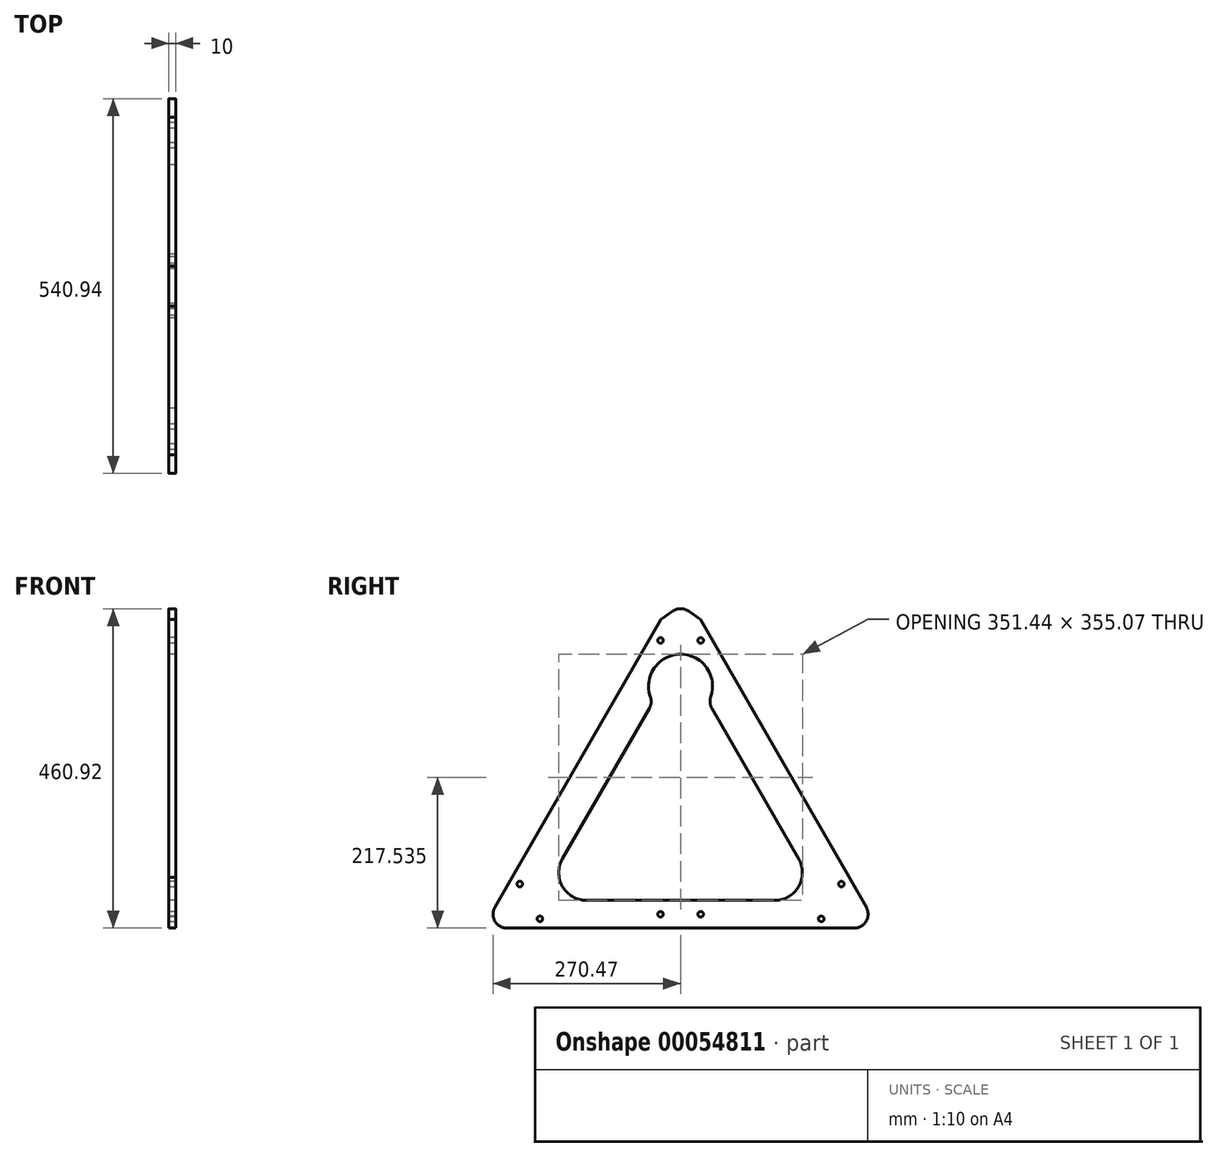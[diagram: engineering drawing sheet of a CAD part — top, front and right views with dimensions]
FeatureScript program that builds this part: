
annotation { "Feature Type Name" : "Feature", "Feature Type Description" : "" }
export const myFeature = defineFeature(function(context is Context, id is Id, definition is map)
    precondition{}
    {
        {
            var Q0;
            Q0=qCreatedBy(makeId("Right.planeOp"),FACE);
            var sketch = newSketch(context, id + "F0", { "sketchPlane" : qUnion([Q0])});
            skLineSegment(sketch, "E0", {"start": v(-103.88, 0) * mm, "end": v(158.82, 0) * mm, "construction": true});
            skLineSegment(sketch, "E1", {"start": v(0, 81.5) * mm, "end": v(0, -83.4) * mm, "construction": true});
            skLineSegment(sketch, "E2.0", {"start": v(-145, 81.5) * mm, "end": v(-145, -83.4) * mm, "construction": true});
            skLineSegment(sketch, "E3.0", {"start": v(-205, 81.5) * mm, "end": v(-205, -83.4) * mm, "construction": true});
            skLineSegment(sketch, "E4.0", {"start": v(-145, -40) * mm, "end": v(145, -40) * mm, "construction": true});
            skLineSegment(sketch, "E5", {"start": v(0, 0) * mm, "end": v(-205, 0) * mm, "construction": true});
            skLineSegment(sketch, "E6", {"start": v(-205, 0) * mm, "end": v(-195.15, 17.07) * mm, "construction": true});
            skLineSegment(sketch, "E7", {"start": v(-205, 0) * mm, "end": v(-200.07, 8.53) * mm, "construction": true});
            skLineSegment(sketch, "E8", {"start": v(-200.07, 8.53) * mm, "end": v(14.56, 380.29) * mm, "construction": true});
            skLineSegment(sketch, "E9", {"start": v(0, 0) * mm, "end": v(0, 452.2) * mm, "construction": true});
            skSolve(sketch);
        }
        {
            var Q0;
            Q0=qCreatedBy(makeId("Right.planeOp"),FACE);
            var sketch = newSketch(context, id + "F1", { "sketchPlane" : qUnion([Q0])});
            skLineSegment(sketch, "E10.0", {"start": v(0, 0) * mm, "end": v(-205, 0) * mm});
            skLineSegment(sketch, "E11.0", {"start": v(-200.07, 8.53) * mm, "end": v(0, 355.07) * mm});
            skLineSegment(sketch, "E12.0", {"start": v(-145, -40) * mm, "end": v(145, -40) * mm});
            skLineSegment(sketch, "E13.0", {"start": v(0, 81.5) * mm, "end": v(0, 0) * mm});
            skLineSegment(sketch, "E14", {"start": v(0, -83.4) * mm, "end": v(0, 81.5) * mm, "construction": true});
            skLineSegment(sketch, "E15", {"start": v(0, -40) * mm, "end": v(-384.65, -40) * mm, "construction": true});
            skLineSegment(sketch, "E16.0", {"start": v(-243.37, 33.53) * mm, "end": v(-28.74, 405.29) * mm, "construction": true});
            skLineSegment(sketch, "E17", {"start": v(-145, -40) * mm, "end": v(-284.62, -40) * mm, "construction": true});
            skLineSegment(sketch, "E18", {"start": v(-284.62, -40) * mm, "end": v(-243.37, 33.53) * mm});
            skLineSegment(sketch, "E19", {"start": v(-243.37, 33.53) * mm, "end": v(-28.74, 405.29) * mm});
            skLineSegment(sketch, "E20", {"start": v(-28.74, 405.29) * mm, "end": v(0, 425.28) * mm});
            skLineSegment(sketch, "E21", {"start": v(-200.07, 8.53) * mm, "end": v(-205, 0) * mm});
            skLineSegment(sketch, "E22", {"start": v(-44.8, 433.21) * mm, "end": v(-37.84, 423.2) * mm});
            skLineSegment(sketch, "E23", {"start": v(-284.62, -40) * mm, "end": v(0, -40) * mm});
            skLineSegment(sketch, "E24.MirrorCS", {"start": v(243.37, 33.53) * mm, "end": v(28.74, 405.29) * mm});
            skLineSegment(sketch, "E25.MirrorCS", {"start": v(28.74, 405.29) * mm, "end": v(0, 425.28) * mm});
            skLineSegment(sketch, "E26.MirrorCS", {"start": v(200.07, 8.53) * mm, "end": v(0, 355.07) * mm});
            skLineSegment(sketch, "E27.MirrorCS", {"start": v(284.62, -40) * mm, "end": v(243.37, 33.53) * mm});
            skLineSegment(sketch, "E28.MirrorCS", {"start": v(284.62, -40) * mm, "end": v(0, -40) * mm});
            skLineSegment(sketch, "E29.MirrorCS", {"start": v(0, 0) * mm, "end": v(205, 0) * mm});
            skLineSegment(sketch, "E30.MirrorCS", {"start": v(200.07, 8.53) * mm, "end": v(205, 0) * mm});
            skLineSegment(sketch, "E31.trimOffspring", {"start": v(0, -40) * mm, "end": v(0, -83.4) * mm});
            skPoint(sketch, "E32.orphan", {"position": v(-14.56, 380.29) * mm});
            skPoint(sketch, "E33.orphan", {"position": v(14.56, 380.29) * mm});
            skLineSegment(sketch, "E34", {"start": v(0, 355.07) * mm, "end": v(-80.62, 355.07) * mm, "construction": true});
            skLineSegment(sketch, "E35", {"start": v(0, 355.07) * mm, "end": v(0, 406.28) * mm, "construction": true});
            skLineSegment(sketch, "E36.0", {"start": v(-29, 355.07) * mm, "end": v(-29, 406.28) * mm, "construction": true});
            skLineSegment(sketch, "E37", {"start": v(0, 355.07) * mm, "end": v(0, 0) * mm, "construction": true});
            skLineSegment(sketch, "E38", {"start": v(0, 177.54) * mm, "end": v(340.97, 177.54) * mm, "construction": true});
            skLineSegment(sketch, "E39.0", {"start": v(-40, 355.07) * mm, "end": v(-40, 0) * mm, "construction": true});
            skLineSegment(sketch, "E40", {"start": v(-40, 285.79) * mm, "end": v(0, 285.79) * mm, "construction": true});
            skLineSegment(sketch, "E41.0", {"start": v(-40, 335.79) * mm, "end": v(0, 335.79) * mm, "construction": true});
            skArc(sketch, "E42", {"start": v(0, 355.07) * mm, "mid": v(-40, 331.98) * mm, "end": v(-40, 285.79) * mm});
            skArc(sketch, "E43.MirrorCS", {"start": v(0, 355.07) * mm, "mid": v(40, 331.98) * mm, "end": v(40, 285.79) * mm});
            skLineSegment(sketch, "E44.0", {"start": v(0, 375.07) * mm, "end": v(-80.62, 375.07) * mm, "construction": true});
            skCircle(sketch, "E45", {"center": v(-29, 375.07) * mm, "radius": 4 * mm});
            skCircle(sketch, "E46.MirrorC", {"center": v(29, 375.07) * mm, "radius": 4 * mm});
            skCircle(sketch, "E47.1.0", {"center": v(-231.93, 23.58) * mm, "radius": 4 * mm});
            skCircle(sketch, "E47.1.1", {"center": v(-202.93, -26.65) * mm, "radius": 4 * mm});
            skCircle(sketch, "E47.2.0", {"center": v(202.93, -26.65) * mm, "radius": 4 * mm});
            skCircle(sketch, "E47.2.1", {"center": v(231.93, 23.58) * mm, "radius": 4 * mm});
            skPoint(sketch, "E47.center", {"position": v(0, 124) * mm});
            skPoint(sketch, "E48.MirrorP", {"position": v(14.56, -25.22) * mm});
            skPoint(sketch, "E49.MirrorP", {"position": v(-14.56, -25.22) * mm});
            skCircle(sketch, "E50.MirrorC", {"center": v(29, -20) * mm, "radius": 4 * mm});
            skCircle(sketch, "E51.MirrorC", {"center": v(-29, -20) * mm, "radius": 4 * mm});
            skSolve(sketch);
        }
        {
            var Q0;
            Q0=makeQuery(id+"F1.imprint","IMPRINT",FACE,{"disambiguationData":[TD([[makeQuery(id+"F1.imprint","IMPRINT",EDGE,{"derivedFrom":sQuery(id+"F1.wireOp",EDGE,"E10.0")}),1.0]])]});
            extrude(context, id + "F2", {"entities" : qUnion([Q0]), "depth" : 10 * mm, "offsetDistance" : 25 * mm});
        }
        {
            var Q0;
            Q0=makeQuery(id+"F2.opExtrude","SWEPT_EDGE",EDGE,{"disambiguationData":[OSD([sQuery(id+"F1.wireOp",EDGE,"E18"),sQuery(id+"F1.wireOp",EDGE,"E23")])]});
            var Q1;
            Q1=makeQuery(id+"F2.opExtrude","SWEPT_EDGE",EDGE,{"disambiguationData":[OSD([sQuery(id+"F1.wireOp",EDGE,"E27.MirrorCS"),sQuery(id+"F1.wireOp",EDGE,"E28.MirrorCS")])]});
            var Q2;
            Q2=makeQuery(id+"F2.opExtrude","SWEPT_EDGE",EDGE,{"disambiguationData":[OSD([sQuery(id+"F1.wireOp",EDGE,"E20"),sQuery(id+"F1.wireOp",EDGE,"E25.MirrorCS")])]});
            var Q3;
            Q3=makeQuery(id+"F2.opExtrude","SWEPT_EDGE",EDGE,{"disambiguationData":[OSD([sQuery(id+"F1.wireOp",EDGE,"E11.0"),sQuery(id+"F1.wireOp",EDGE,"E42")])]});
            var Q4;
            Q4=makeQuery(id+"F2.opExtrude","SWEPT_EDGE",EDGE,{"disambiguationData":[OSD([sQuery(id+"F1.wireOp",EDGE,"E26.MirrorCS"),sQuery(id+"F1.wireOp",EDGE,"E43.MirrorCS")])]});
            fillet(context, id + "F3", {"entities" : qUnion([Q0, Q1, Q2, Q3, Q4]), "tangentPropagation" : true, "radius" : 20 * mm, "defaultsChanged" : false, "vertexSettings" : [], "allowEdgeOverflow" : false});
        }
        {
            var Q0;
            Q0=makeQuery(id+"F2.opExtrude","SWEPT_EDGE",EDGE,{"disambiguationData":[OSD([sQuery(id+"F1.wireOp",EDGE,"E29.MirrorCS"),sQuery(id+"F1.wireOp",EDGE,"E30.MirrorCS")])]});
            var Q1;
            Q1=makeQuery(id+"F2.opExtrude","SWEPT_EDGE",EDGE,{"disambiguationData":[OSD([sQuery(id+"F1.wireOp",EDGE,"E10.0"),sQuery(id+"F1.wireOp",EDGE,"E21")])]});
            fillet(context, id + "F4", {"entities" : qUnion([Q0, Q1]), "tangentPropagation" : true, "radius" : 40 * mm, "defaultsChanged" : true, "vertexSettings" : [], "allowEdgeOverflow" : false});
        }
    });
